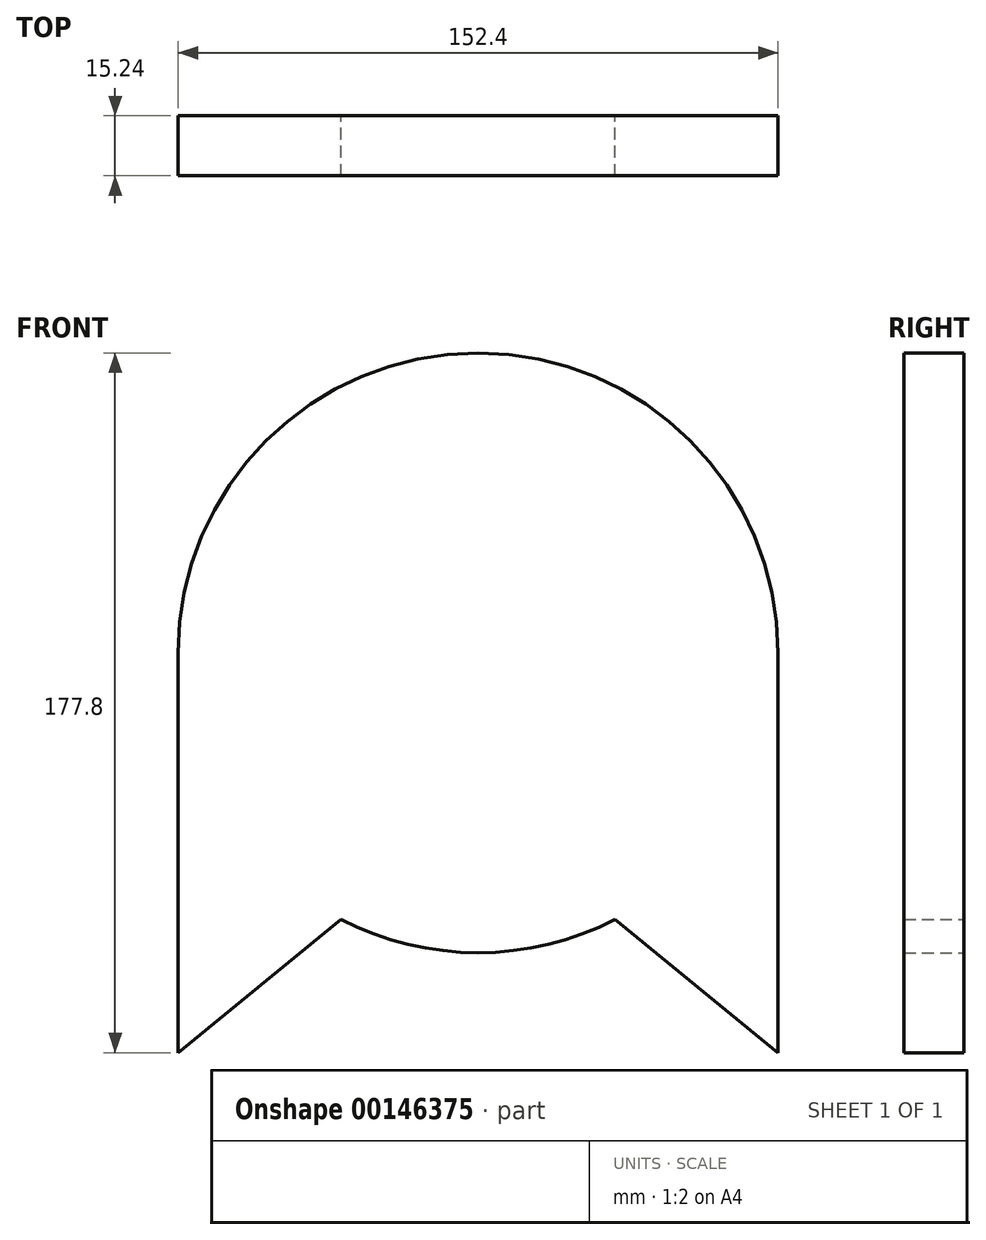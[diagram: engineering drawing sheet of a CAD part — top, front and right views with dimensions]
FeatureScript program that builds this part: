
annotation { "Feature Type Name" : "Feature", "Feature Type Description" : "" }
export const myFeature = defineFeature(function(context is Context, id is Id, definition is map)
    precondition{}
    {
        {
            var Q0;
            Q0=qCreatedBy(makeId("Front.planeOp"),FACE);
            var sketch = newSketch(context, id + "F0", { "sketchPlane" : qUnion([Q0])});
            skCircle(sketch, "E0", {"center": v(0, 0) * mm, "radius": 76.2 * mm});
            skLineSegment(sketch, "E1", {"start": v(-76.2, 0) * mm, "end": v(-76.2, -101.6) * mm});
            skLineSegment(sketch, "E2", {"start": v(76.2, 0) * mm, "end": v(76.2, -101.6) * mm});
            skLineSegment(sketch, "E3", {"start": v(76.2, -101.6) * mm, "end": v(34.79, -67.8) * mm});
            skLineSegment(sketch, "E4", {"start": v(-76.2, -101.6) * mm, "end": v(-34.79, -67.8) * mm});
            skSolve(sketch);
        }
        {
            var Q0;
            {var subQ0=sQuery(id+"F0.wireOp",EDGE,"VfDvaqEg-P0tx-Wh4J-oVVj-PGz4n2cgn3sZ.left");Q0=makeQuery(id+"F0.imprint","IMPRINT",FACE,{"disambiguationData":[TD([[makeQuery(id+"F0.imprint","IMPRINT",EDGE,{"derivedFrom":subQ0}),1.0]])]});}
            var Q1;
            {var subQ0=sQuery(id+"F0.wireOp",EDGE,"VfDvaqEg-P0tx-Wh4J-oVVj-PGz4n2cgn3sZ.right");Q1=makeQuery(id+"F0.imprint","IMPRINT",FACE,{"disambiguationData":[TD([[makeQuery(id+"F0.imprint","IMPRINT",EDGE,{"derivedFrom":subQ0}),-1.0]])]});}
            var Q2;
            {var subQ0=sQuery(id+"F0.wireOp",EDGE,"E0");var subQ1=makeQuery(id+"F0.imprint","INTERSECT",VERTEX,{"derivedFrom":[subQ0,sQuery(id+"F0.wireOp",EDGE,"VfDvaqEg-P0tx-Wh4J-oVVj-PGz4n2cgn3sZ.left")]});Q2=makeQuery(id+"F0.imprint","IMPRINT",FACE,{"disambiguationData":[TD([[makeQuery(id+"F0.imprint","IMPRINT",EDGE,{"disambiguationData":[TD([[subQ1,1.0]])],"derivedFrom":subQ0}),1.0]])]});}
            var Q3;
            {var subQ0=sQuery(id+"F0.wireOp",EDGE,"E1");Q3=makeQuery(id+"F0.imprint","IMPRINT",FACE,{"disambiguationData":[TD([[makeQuery(id+"F0.imprint","IMPRINT",EDGE,{"derivedFrom":subQ0}),1.0]])]});}
            var Q4;
            {var subQ0=sQuery(id+"F0.wireOp",EDGE,"E2");Q4=makeQuery(id+"F0.imprint","IMPRINT",FACE,{"disambiguationData":[TD([[makeQuery(id+"F0.imprint","IMPRINT",EDGE,{"derivedFrom":subQ0}),-1.0]])]});}
            extrude(context, id + "F1", {"entities" : qUnion([Q0, Q1, Q2, Q3, Q4]), "depth" : 15.24 * mm});
        }
    });
